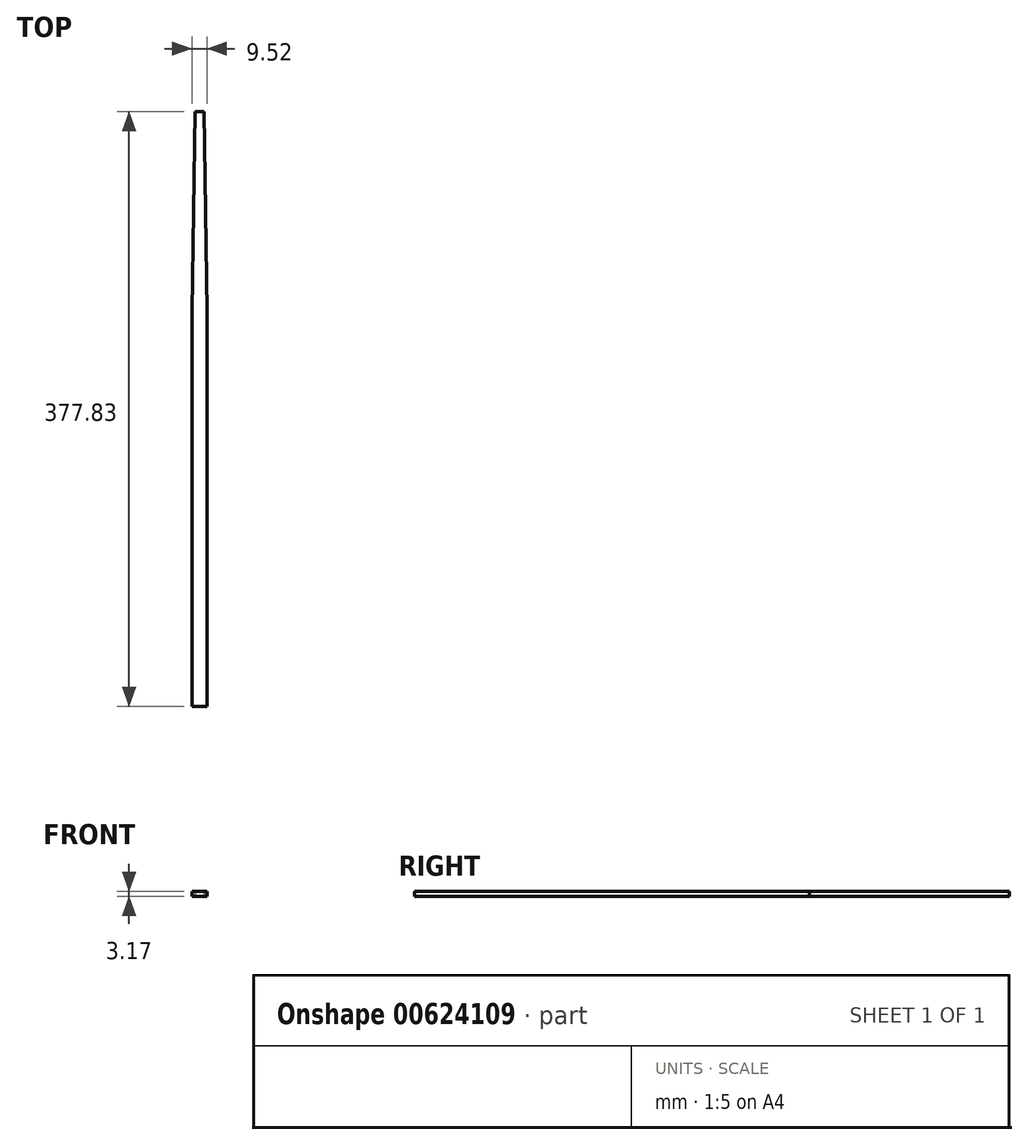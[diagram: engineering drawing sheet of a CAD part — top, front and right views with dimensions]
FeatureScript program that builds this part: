
annotation { "Feature Type Name" : "Feature", "Feature Type Description" : "" }
export const myFeature = defineFeature(function(context is Context, id is Id, definition is map)
    precondition{}
    {
        {
            var Q0;
            Q0=qCreatedBy(makeId("Top.planeOp"),FACE);
            var sketch = newSketch(context, id + "F0", { "sketchPlane" : qUnion([Q0])});
            skLineSegment(sketch, "E0.bottom", {"start": v(-42.67, 330.07) * mm, "end": v(-37.03, 330.07) * mm});
            skLineSegment(sketch, "E0.top", {"start": v(-44.61, -47.76) * mm, "end": v(-35.09, -47.76) * mm});
            skLineSegment(sketch, "E0.left", {"start": v(-44.61, 203.06) * mm, "end": v(-44.61, -47.76) * mm});
            skLineSegment(sketch, "E0.right", {"start": v(-35.09, 203.06) * mm, "end": v(-35.09, -47.76) * mm});
            skLineSegment(sketch, "E1", {"start": v(-42.67, 330.07) * mm, "end": v(-44.61, 203.06) * mm});
            skLineSegment(sketch, "E2", {"start": v(-37.03, 330.07) * mm, "end": v(-35.09, 203.06) * mm});
            skPoint(sketch, "E3.orphan", {"position": v(-44.61, 330.07) * mm});
            skPoint(sketch, "E4.orphan", {"position": v(-35.09, 330.07) * mm});
            skSolve(sketch);
        }
        {
            var Q0;
            Q0=makeQuery(id+"F0.imprint","IMPRINT",FACE,{"disambiguationData":[TD([[makeQuery(id+"F0.imprint","IMPRINT",EDGE,{"derivedFrom":sQuery(id+"F0.wireOp",EDGE,"E0.bottom")}),-1.0]])]});
            extrude(context, id + "F1", {"entities" : qUnion([Q0]), "depth" : 3.17 * mm, "offsetDistance" : 25.4 * mm});
        }
    });
